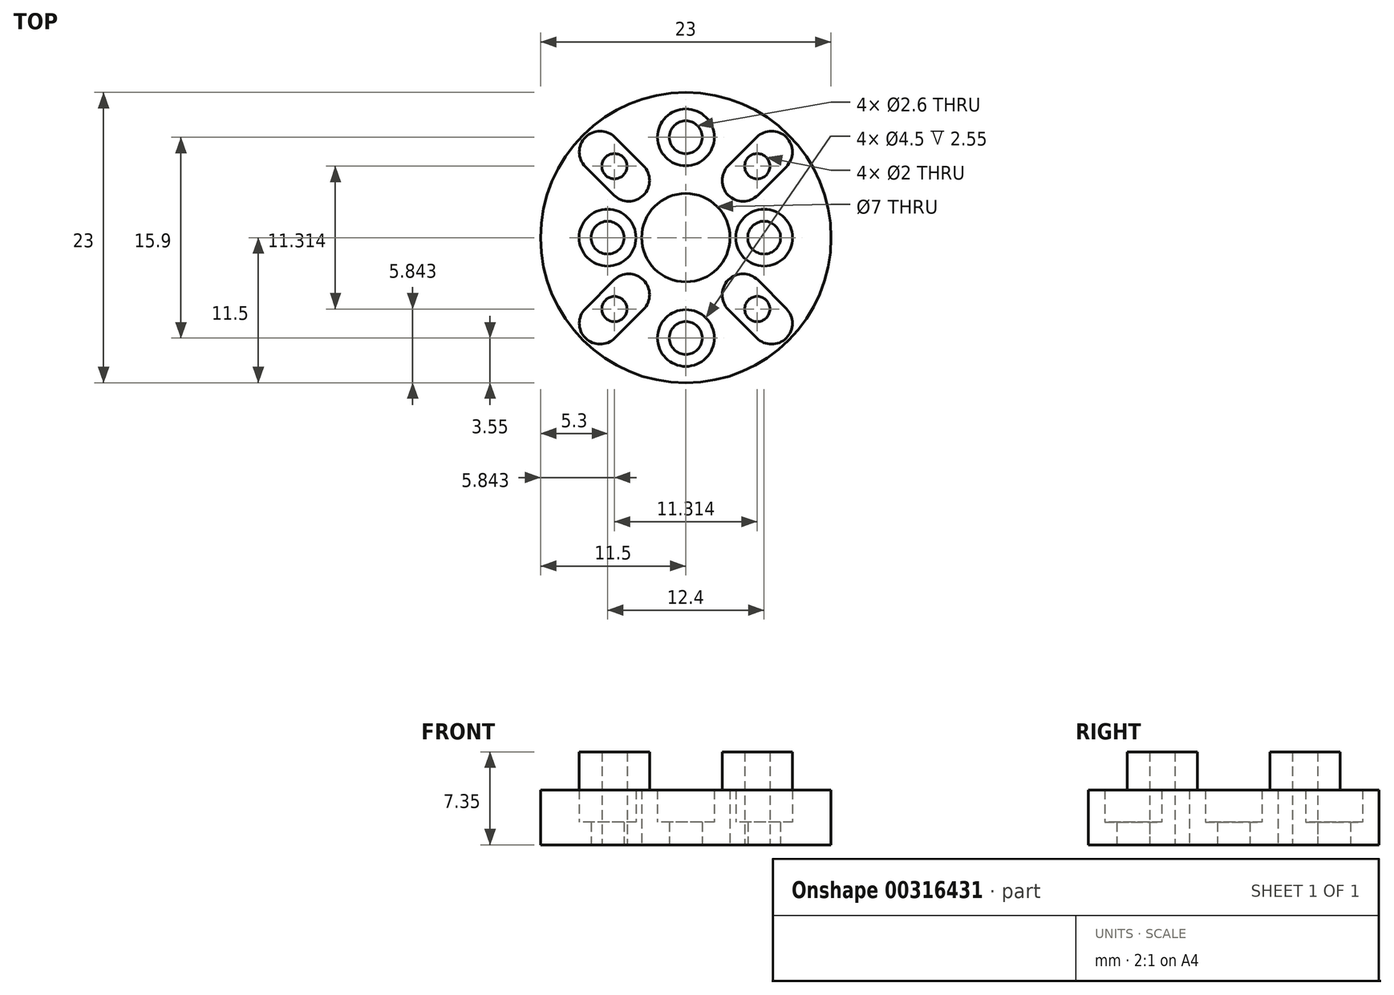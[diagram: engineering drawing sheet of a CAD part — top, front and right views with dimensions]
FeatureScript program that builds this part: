
annotation { "Feature Type Name" : "Feature", "Feature Type Description" : "" }
export const myFeature = defineFeature(function(context is Context, id is Id, definition is map)
    precondition{}
    {
        {
            var Q0;
            Q0=qCreatedBy(makeId("Top.planeOp"),FACE);
            var sketch = newSketch(context, id + "F0", { "sketchPlane" : qUnion([Q0])});
            skCircle(sketch, "E0", {"center": v(0, 0) * mm, "radius": 11.5 * mm});
            skCircle(sketch, "E1", {"center": v(0, 0) * mm, "radius": 3.5 * mm});
            skCircle(sketch, "E2", {"center": v(6.2, 0) * mm, "radius": 1.3 * mm});
            skCircle(sketch, "E3", {"center": v(-6.2, 0) * mm, "radius": 1.3 * mm});
            skCircle(sketch, "E4", {"center": v(0, 7.95) * mm, "radius": 1.3 * mm});
            skCircle(sketch, "E5", {"center": v(0, -7.95) * mm, "radius": 1.3 * mm});
            skSolve(sketch);
        }
        {
            var Q0;
            Q0 = qSketchRegion(id + "F0", true);
            extrude(context, id + "F1", {"entities" : qUnion([Q0]), "depth" : 4.35 * mm});
        }
        {
            var Q0;
            Q0=qCreatedBy(makeId("Top.planeOp"),FACE);
            cPlane(context, id + "F2", {"entities" : qUnion([Q0]), "cplaneType" : CPlaneType.OFFSET, "offset" : 4.35 * mm, "width" : 150 * mm, "height" : 150 * mm});
        }
        {
            var Q0;
            Q0=qCreatedBy(id+"F2.planeOp",FACE);
            var sketch = newSketch(context, id + "F3", { "sketchPlane" : qUnion([Q0])});
            skLineSegment(sketch, "E6", {"start": v(0, 0) * mm, "end": v(4.53, -4.53) * mm, "construction": true});
            skLineSegment(sketch, "E7", {"start": v(0, 0) * mm, "end": v(4.53, 4.53) * mm, "construction": true});
            skLineSegment(sketch, "E8", {"start": v(4.53, -4.53) * mm, "end": v(6.79, -6.79) * mm});
            skArc(sketch, "E9.0.startCap", {"start": v(3.36, -5.7) * mm, "mid": v(3.36, -3.36) * mm, "end": v(5.7, -3.36) * mm});
            skArc(sketch, "E9.0.endCap", {"start": v(7.95, -5.62) * mm, "mid": v(7.95, -7.95) * mm, "end": v(5.62, -7.95) * mm});
            skLineSegment(sketch, "E9.0.left", {"start": v(5.7, -3.36) * mm, "end": v(7.95, -5.62) * mm});
            skLineSegment(sketch, "E9.0.right", {"start": v(3.36, -5.7) * mm, "end": v(5.62, -7.95) * mm});
            skLineSegment(sketch, "E10.MirrorCS", {"start": v(4.53, 4.53) * mm, "end": v(6.79, 6.79) * mm});
            skLineSegment(sketch, "E11.MirrorCS", {"start": v(-4.53, 4.53) * mm, "end": v(-6.79, 6.79) * mm});
            skLineSegment(sketch, "E12.MirrorCS", {"start": v(-4.53, -4.53) * mm, "end": v(-6.79, -6.79) * mm});
            skArc(sketch, "E13.0.startCap", {"start": v(5.7, 3.36) * mm, "mid": v(3.36, 3.36) * mm, "end": v(3.36, 5.7) * mm});
            skArc(sketch, "E13.0.endCap", {"start": v(5.62, 7.95) * mm, "mid": v(7.95, 7.95) * mm, "end": v(7.95, 5.62) * mm});
            skLineSegment(sketch, "E13.0.left", {"start": v(3.36, 5.7) * mm, "end": v(5.62, 7.95) * mm});
            skLineSegment(sketch, "E13.0.right", {"start": v(5.7, 3.36) * mm, "end": v(7.95, 5.62) * mm});
            skArc(sketch, "E13.1.startCap", {"start": v(-3.36, 5.7) * mm, "mid": v(-3.36, 3.36) * mm, "end": v(-5.7, 3.36) * mm});
            skArc(sketch, "E13.1.endCap", {"start": v(-7.95, 5.62) * mm, "mid": v(-7.95, 7.95) * mm, "end": v(-5.62, 7.95) * mm});
            skLineSegment(sketch, "E13.1.left", {"start": v(-5.7, 3.36) * mm, "end": v(-7.95, 5.62) * mm});
            skLineSegment(sketch, "E13.1.right", {"start": v(-3.36, 5.7) * mm, "end": v(-5.62, 7.95) * mm});
            skArc(sketch, "E13.2.startCap", {"start": v(-5.7, -3.36) * mm, "mid": v(-3.36, -3.36) * mm, "end": v(-3.36, -5.7) * mm});
            skArc(sketch, "E13.2.endCap", {"start": v(-5.62, -7.95) * mm, "mid": v(-7.95, -7.95) * mm, "end": v(-7.95, -5.62) * mm});
            skLineSegment(sketch, "E13.2.left", {"start": v(-3.36, -5.7) * mm, "end": v(-5.62, -7.95) * mm});
            skLineSegment(sketch, "E13.2.right", {"start": v(-5.7, -3.36) * mm, "end": v(-7.95, -5.62) * mm});
            skSolve(sketch);
        }
        {
            var Q0;
            Q0 = qSketchRegion(id + "F3", true);
            extrude(context, id + "F4", {"entities" : qUnion([Q0]), "operationType" : NewBodyOperationType.ADD, "depth" : 3 * mm});
        }
        {
            var Q0;
            Q0=qCreatedBy(makeId("Top.planeOp"),FACE);
            cPlane(context, id + "F5", {"entities" : qUnion([Q0]), "cplaneType" : CPlaneType.OFFSET, "offset" : 1.8 * mm, "width" : 150 * mm, "height" : 150 * mm});
        }
        {
            var Q0;
            Q0=qCreatedBy(id+"F5.planeOp",FACE);
            var sketch = newSketch(context, id + "F6", { "sketchPlane" : qUnion([Q0])});
            skCircle(sketch, "E14", {"center": v(0, -7.95) * mm, "radius": 2.25 * mm});
            skCircle(sketch, "E15", {"center": v(6.2, 0) * mm, "radius": 2.25 * mm});
            skCircle(sketch, "E16", {"center": v(0, 7.95) * mm, "radius": 2.25 * mm});
            skCircle(sketch, "E17", {"center": v(-6.2, 0) * mm, "radius": 2.25 * mm});
            skSolve(sketch);
        }
        {
            var Q0;
            Q0 = qSketchRegion(id + "F6", true);
            extrude(context, id + "F7", {"entities" : qUnion([Q0]), "operationType" : NewBodyOperationType.REMOVE, "oppositeDirection" : true, "depth" : -2.6 * mm});
        }
        {
            var Q0;
            Q0=qCreatedBy(makeId("Top.planeOp"),FACE);
            var sketch = newSketch(context, id + "F8", { "sketchPlane" : qUnion([Q0])});
            skCircle(sketch, "E18", {"center": v(5.66, -5.66) * mm, "radius": 1 * mm});
            skCircle(sketch, "E19", {"center": v(5.66, 5.66) * mm, "radius": 1 * mm});
            skCircle(sketch, "E20", {"center": v(-5.66, 5.66) * mm, "radius": 1 * mm});
            skCircle(sketch, "E21", {"center": v(-5.66, -5.66) * mm, "radius": 1 * mm});
            skLineSegment(sketch, "E22", {"start": v(-5.66, 5.66) * mm, "end": v(0, 0) * mm, "construction": true});
            skLineSegment(sketch, "E23", {"start": v(0, 0) * mm, "end": v(-5.66, -5.66) * mm, "construction": true});
            skLineSegment(sketch, "E24", {"start": v(5.66, 5.66) * mm, "end": v(0, 0) * mm, "construction": true});
            skLineSegment(sketch, "E25", {"start": v(5.66, -5.66) * mm, "end": v(0, 0) * mm, "construction": true});
            skSolve(sketch);
        }
        {
            var Q0;
            Q0 = qSketchRegion(id + "F8", true);
            extrude(context, id + "F9", {"entities" : qUnion([Q0]), "operationType" : NewBodyOperationType.REMOVE, "depth" : 8 * mm});
        }
    });
